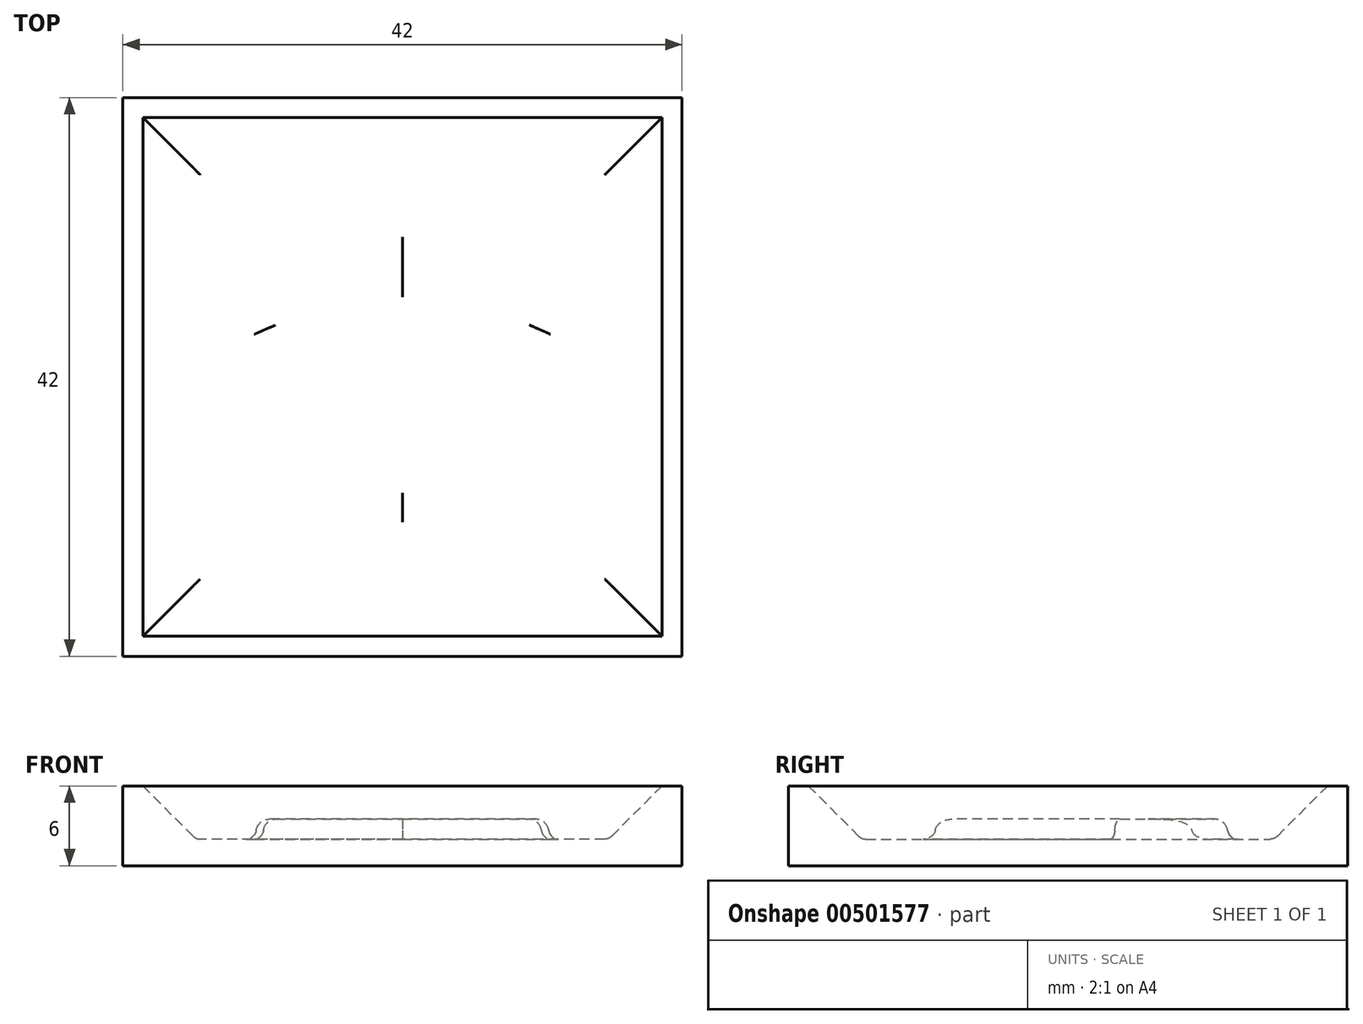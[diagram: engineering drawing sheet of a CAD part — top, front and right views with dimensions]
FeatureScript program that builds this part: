
annotation { "Feature Type Name" : "Feature", "Feature Type Description" : "" }
export const myFeature = defineFeature(function(context is Context, id is Id, definition is map)
    precondition{}
    {
        {
            var Q0;
            Q0=qCreatedBy(makeId("Top.planeOp"),FACE);
            var sketch = newSketch(context, id + "F0", { "sketchPlane" : qUnion([Q0])});
            skLineSegment(sketch, "E0.bottom", {"start": v(-21, 21) * mm, "end": v(21, 21) * mm});
            skLineSegment(sketch, "E0.top", {"start": v(-21, -21) * mm, "end": v(21, -21) * mm});
            skLineSegment(sketch, "E0.left", {"start": v(-21, 21) * mm, "end": v(-21, -21) * mm});
            skLineSegment(sketch, "E0.right", {"start": v(21, 21) * mm, "end": v(21, -21) * mm});
            skSolve(sketch);
        }
        {
            var Q0;
            Q0=qSketchRegion(id+"F0",true);
            extrude(context, id + "F1", {"entities" : qUnion([Q0]), "depth" : 2 * mm});
        }
        {
            var Q0;
            Q0=makeQuery(id+"F1.opExtrude","CAP_FACE",FACE,{"disambiguationData":[OSD([sQuery(id+"F0.wireOp",EDGE,"E0.bottom"),sQuery(id+"F0.wireOp",EDGE,"E0.top"),sQuery(id+"F0.wireOp",EDGE,"E0.left"),sQuery(id+"F0.wireOp",EDGE,"E0.right")])],"isStart":false});
            var sketch = newSketch(context, id + "F2", { "sketchPlane" : qUnion([Q0])});
            skLineSegment(sketch, "E1.bottom", {"start": v(-21, 21) * mm, "end": v(21, 21) * mm});
            skLineSegment(sketch, "E1.top", {"start": v(-21, -21) * mm, "end": v(21, -21) * mm});
            skLineSegment(sketch, "E1.left", {"start": v(-21, 21) * mm, "end": v(-21, -21) * mm});
            skLineSegment(sketch, "E1.right", {"start": v(21, 21) * mm, "end": v(21, -21) * mm});
            skLineSegment(sketch, "E2.bottom", {"start": v(-15.5, 15.5) * mm, "end": v(15.5, 15.5) * mm});
            skLineSegment(sketch, "E2.top", {"start": v(-15.5, -15.5) * mm, "end": v(15.5, -15.5) * mm});
            skLineSegment(sketch, "E2.left", {"start": v(-15.5, 15.5) * mm, "end": v(-15.5, -15.5) * mm});
            skLineSegment(sketch, "E2.right", {"start": v(15.5, 15.5) * mm, "end": v(15.5, -15.5) * mm});
            skSolve(sketch);
        }
        {
            var Q0;
            Q0=qSketchRegion(id+"F2",true);
            extrude(context, id + "F3", {"entities" : qUnion([Q0]), "operationType" : NewBodyOperationType.ADD, "depth" : 4 * mm});
        }
        {
            var Q0;
            Q0=makeQuery(id+"F3.opExtrude","CAP_EDGE",EDGE,{"disambiguationData":[OSD([sQuery(id+"F2.wireOp",EDGE,"E2.left")])],"isStart":false});
            var Q1;
            Q1=makeQuery(id+"F3.opExtrude","CAP_EDGE",EDGE,{"disambiguationData":[OSD([sQuery(id+"F2.wireOp",EDGE,"E2.bottom")])],"isStart":false});
            var Q2;
            Q2=makeQuery(id+"F3.opExtrude","CAP_EDGE",EDGE,{"disambiguationData":[OSD([sQuery(id+"F2.wireOp",EDGE,"E2.right")])],"isStart":false});
            var Q3;
            Q3=makeQuery(id+"F3.opExtrude","CAP_EDGE",EDGE,{"disambiguationData":[OSD([sQuery(id+"F2.wireOp",EDGE,"E2.top")])],"isStart":false});
            chamfer(context, id + "F4", {"entities" : qUnion([Q0, Q1, Q2, Q3]), "width" : 4 * mm, "tangentPropagation" : true});
        }
        {
            var Q0;
            Q0=makeQuery(id+"F1.opExtrude","CAP_FACE",FACE,{"disambiguationData":[OSD([sQuery(id+"F0.wireOp",EDGE,"E0.bottom"),sQuery(id+"F0.wireOp",EDGE,"E0.top"),sQuery(id+"F0.wireOp",EDGE,"E0.left"),sQuery(id+"F0.wireOp",EDGE,"E0.right")])],"isStart":false});
            var sketch = newSketch(context, id + "F5", { "sketchPlane" : qUnion([Q0])});
            skArc(sketch, "E3", {"start": v(-10.45, 3.5) * mm, "mid": v(-6.1, -3.93) * mm, "end": v(0, -10) * mm});
            skArc(sketch, "E4", {"start": v(0, 9.32) * mm, "mid": v(-7.92, 11.24) * mm, "end": v(-10.45, 3.5) * mm});
            skArc(sketch, "E5.MirrorCS", {"start": v(0, 9.32) * mm, "mid": v(7.92, 11.24) * mm, "end": v(10.45, 3.5) * mm});
            skArc(sketch, "E6.MirrorCS", {"start": v(10.45, 3.5) * mm, "mid": v(6.1, -3.93) * mm, "end": v(0, -10) * mm});
            skSolve(sketch);
        }
        {
            var Q0;
            Q0 = qSketchRegion(id + "F5", true);
            extrude(context, id + "F6", {"entities" : qUnion([Q0]), "operationType" : NewBodyOperationType.ADD, "depth" : 1.5 * mm});
        }
        {
            var Q0;
            Q0=makeQuery(id+"F6.opExtrude","CAP_EDGE",EDGE,{"disambiguationData":[OSD([sQuery(id+"F5.wireOp",EDGE,"E3")])],"isStart":false});
            var Q1;
            Q1=makeQuery(id+"F6.opExtrude","CAP_EDGE",EDGE,{"disambiguationData":[OSD([sQuery(id+"F5.wireOp",EDGE,"E4")])],"isStart":false});
            var Q2;
            Q2=makeQuery(id+"F6.opExtrude","CAP_EDGE",EDGE,{"disambiguationData":[OSD([sQuery(id+"F5.wireOp",EDGE,"E5.MirrorCS")])],"isStart":false});
            fillet(context, id + "F7", {"entities" : qUnion([Q0, Q1, Q2]), "radius" : 1 * mm, "tangentPropagation" : true, "allowEdgeOverflow" : false});
        }
        {
            var Q0;
            Q0=makeQuery(id+"F6.opExtrude","CAP_EDGE",EDGE,{"disambiguationData":[OSD([sQuery(id+"F5.wireOp",EDGE,"E6.MirrorCS")])],"isStart":true});
            var Q1;
            Q1=makeQuery(id+"F1.opExtrude","CAP_FACE",FACE,{"disambiguationData":[OSD([sQuery(id+"F0.wireOp",EDGE,"E0.bottom"),sQuery(id+"F0.wireOp",EDGE,"E0.top"),sQuery(id+"F0.wireOp",EDGE,"E0.left"),sQuery(id+"F0.wireOp",EDGE,"E0.right")])],"isStart":false});
            var Q2;
            Q2=makeQuery(id+"F6.opExtrude","CAP_EDGE",EDGE,{"disambiguationData":[OSD([sQuery(id+"F5.wireOp",EDGE,"E5.MirrorCS")])],"isStart":true});
            fillet(context, id + "F8", {"entities" : qUnion([Q0, Q1, Q2]), "radius" : .75 * mm, "tangentPropagation" : true, "allowEdgeOverflow" : false});
        }
    });
